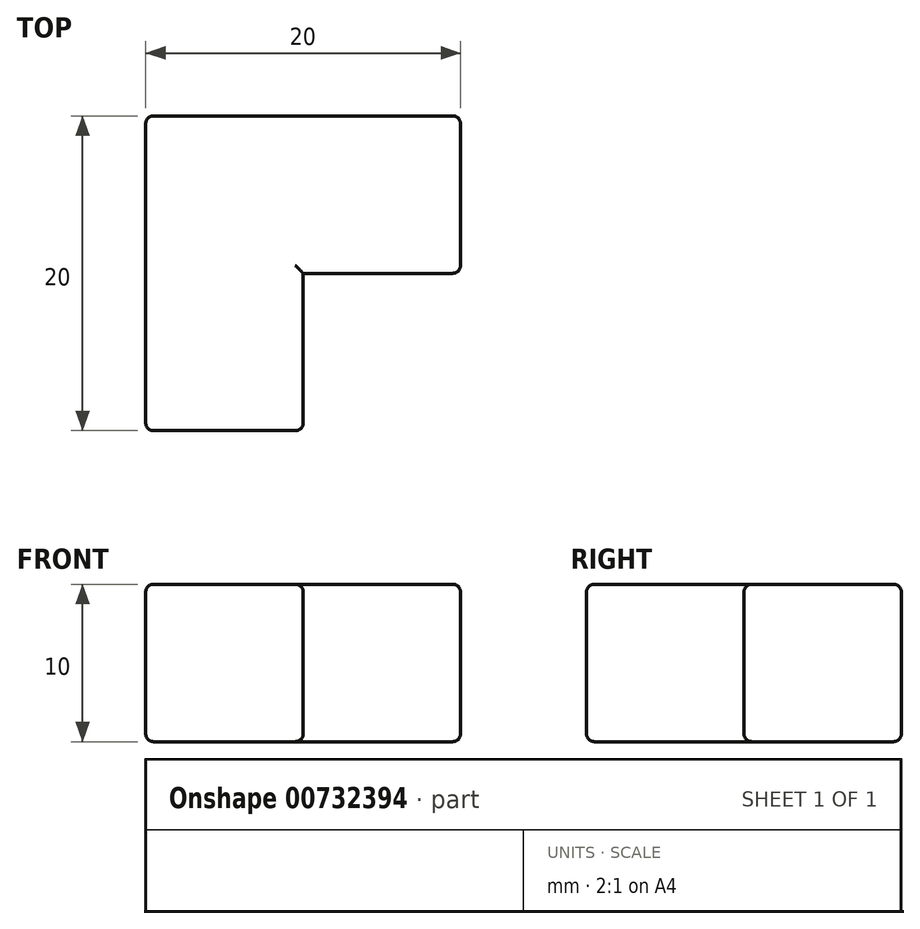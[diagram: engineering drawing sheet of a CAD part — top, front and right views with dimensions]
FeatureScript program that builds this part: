
annotation { "Feature Type Name" : "Feature", "Feature Type Description" : "" }
export const myFeature = defineFeature(function(context is Context, id is Id, definition is map)
    precondition{}
    {
        {
            var Q0;
            Q0=qCreatedBy(makeId("Front.planeOp"),FACE);
            var sketch = newSketch(context, id + "F0", { "sketchPlane" : qUnion([Q0])});
            skLineSegment(sketch, "E0.bottom", {"start": v(10, -5) * mm, "end": v(-10, -5) * mm});
            skLineSegment(sketch, "E0.top", {"start": v(10, 5) * mm, "end": v(-10, 5) * mm});
            skLineSegment(sketch, "E0.left", {"start": v(10, -5) * mm, "end": v(10, 5) * mm});
            skLineSegment(sketch, "E0.right", {"start": v(-10, -5) * mm, "end": v(-10, 5) * mm});
            skPoint(sketch, "E0.middle", {"position": v(0, 0) * mm});
            skLineSegment(sketch, "E1", {"start": v(0, 5) * mm, "end": v(0, -5) * mm});
            skSolve(sketch);
        }
        {
            var Q0;
            {var subQ0=sQuery(id+"F0.wireOp",EDGE,"E0.right");Q0=makeQuery(id+"F0.imprint","IMPRINT",FACE,{"disambiguationData":[TD([[makeQuery(id+"F0.imprint","IMPRINT",EDGE,{"derivedFrom":subQ0}),-1.0]])]});}
            extrude(context, id + "F1", {"entities" : qUnion([Q0]), "depth" : 20 * mm, "offsetDistance" : 25 * mm});
        }
        {
            var Q0;
            Q0 = qSketchRegion(id + "F0", true);
            extrude(context, id + "F2", {"entities" : qUnion([Q0]), "operationType" : NewBodyOperationType.ADD, "depth" : 10 * mm, "offsetDistance" : 25 * mm});
        }
        {
            var Q0;
            {var subQ0=sQuery(id+"F0.wireOp",EDGE,"E0.top");Q0=makeQuery(id+"F2.boolean.opBoolean","MERGE",FACE,{"derivedFrom":[makeQuery(id+"F1.opExtrude","SWEPT_FACE",FACE,{"disambiguationData":[OSD([subQ0])]}),makeQuery(id+"F2.opExtrude","SWEPT_FACE",FACE,{"disambiguationData":[OSD([subQ0])]})]});}
            var Q1;
            {var subQ0=sQuery(id+"F0.wireOp",EDGE,"E0.bottom");Q1=makeQuery(id+"F2.boolean.opBoolean","MERGE",FACE,{"derivedFrom":[makeQuery(id+"F1.opExtrude","SWEPT_FACE",FACE,{"disambiguationData":[OSD([subQ0])]}),makeQuery(id+"F2.opExtrude","SWEPT_FACE",FACE,{"disambiguationData":[OSD([subQ0])]})]});}
            var Q2;
            {var subQ0=sQuery(id+"F0.wireOp",EDGE,"E0.right");var subQ1=sQuery(id+"F0.wireOp",EDGE,"E0.top");var subQ2=sQuery(id+"F0.wireOp",EDGE,"E0.bottom");Q2=makeQuery(id+"F2.boolean.opBoolean","MERGE",FACE,{"derivedFrom":[makeQuery(id+"F1.opExtrude","CAP_FACE",FACE,{"disambiguationData":[OSD([subQ2,subQ1,subQ0,sQuery(id+"F0.wireOp",EDGE,"E1")])],"isStart":true}),makeQuery(id+"F2.opExtrude","CAP_FACE",FACE,{"disambiguationData":[OSD([subQ2,subQ1,sQuery(id+"F0.wireOp",EDGE,"E0.left"),subQ0])],"isStart":true})]});}
            var Q3;
            Q3=makeQuery(id+"F1.opExtrude","CAP_FACE",FACE,{"disambiguationData":[OSD([sQuery(id+"F0.wireOp",EDGE,"E0.bottom"),sQuery(id+"F0.wireOp",EDGE,"E0.top"),sQuery(id+"F0.wireOp",EDGE,"E0.right"),sQuery(id+"F0.wireOp",EDGE,"E1")])],"isStart":false});
            var Q4;
            Q4=makeQuery(id+"F2.opExtrude","SWEPT_FACE",FACE,{"disambiguationData":[OSD([sQuery(id+"F0.wireOp",EDGE,"E0.left")])]});
            fillet(context, id + "F3", {"entities" : qUnion([Q0, Q1, Q2, Q3, Q4]), "radius" : 0.5 * mm, "tangentPropagation" : true, "allowEdgeOverflow" : false});
        }
    });
